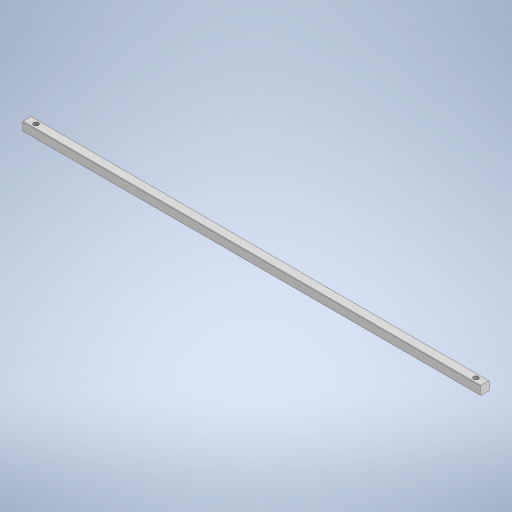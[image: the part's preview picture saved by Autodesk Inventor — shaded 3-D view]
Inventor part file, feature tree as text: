
AUTODESK INVENTOR PART (.ipt)
format: ipt  version: 2024.2 (Build 282272000, 272)  size: 263,680 bytes
history: native  units: in
note: dims shown in document units (in); Inventor stores cm internally (conversion verified against a paired STEP export)
features: extrude x2, thread x2, sketch x2, fillet x1
ambient origin geometry x8: Origin, YZ Plane, XZ Plane, XY Plane, X Axis, Y Axis, Z Axis, Center Point
bodies: Solid1 (feature_tree)
feature tree (7):
  extrude  "Extrusion1"  Depth=0.25in
  fillet  "Fillet1"  Radius=13.0in
  extrude  "Extrusion2"  Depth=0.25in
  thread  "Thread1"  [1 undecoded]
  thread  "Thread2"  [1 undecoded]
  sketch  "Sketch1"  dims[d0=0.25in d1=0.25in d2=13.0in d3=0.0in]
  sketch  "Sketch2"  dims[d4=0.0125in d5=0.1406in d6=0.25in d7=0.1406in d8=0.25in d9=0.25in d10=0.0in d11=0.25in d12=0.0in d13=0.25in d14=0.0in]
note: 2 required parameter values undecoded (feature->parameter linkage not recoverable at this tier; creation-order binding heuristic only, values carry confidence <= 0.55)
